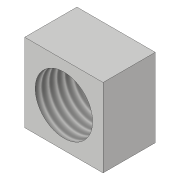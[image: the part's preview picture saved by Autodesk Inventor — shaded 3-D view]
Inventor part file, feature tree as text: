
AUTODESK INVENTOR PART (.ipt)
format: ipt  version: 2019 (Build 230136000, 136)  size: 94,720 bytes
history: native  units: in
note: dims shown in document units (in); Inventor stores cm internally (conversion verified against a paired STEP export)
features: sketch x3, extrude x2, thread x1
ambient origin geometry x8: Origin, YZ Plane, XZ Plane, XY Plane, X Axis, Y Axis, Z Axis, Center Point
bodies: Solid1 (feature_tree)
feature tree (6):
  sketch  "Sketch1"  dims[d0=0.5906in d1=0.5906in]
  extrude  "Extrusion1"  Depth=0.5906in
  extrude  "Extrusion2"  Depth=0.3937in
  thread  "Thread1"  [1 undecoded]
  sketch  "Sketch2"  dims[d2=0.3937in d3=0.0in d4=0.4331in d5=0.0in d6=0.0in]
  sketch  "Sketch3"  dims[d7=0.3937in d8=0.0in]
note: 1 required parameter value undecoded (feature->parameter linkage not recoverable at this tier; creation-order binding heuristic only, values carry confidence <= 0.55)
